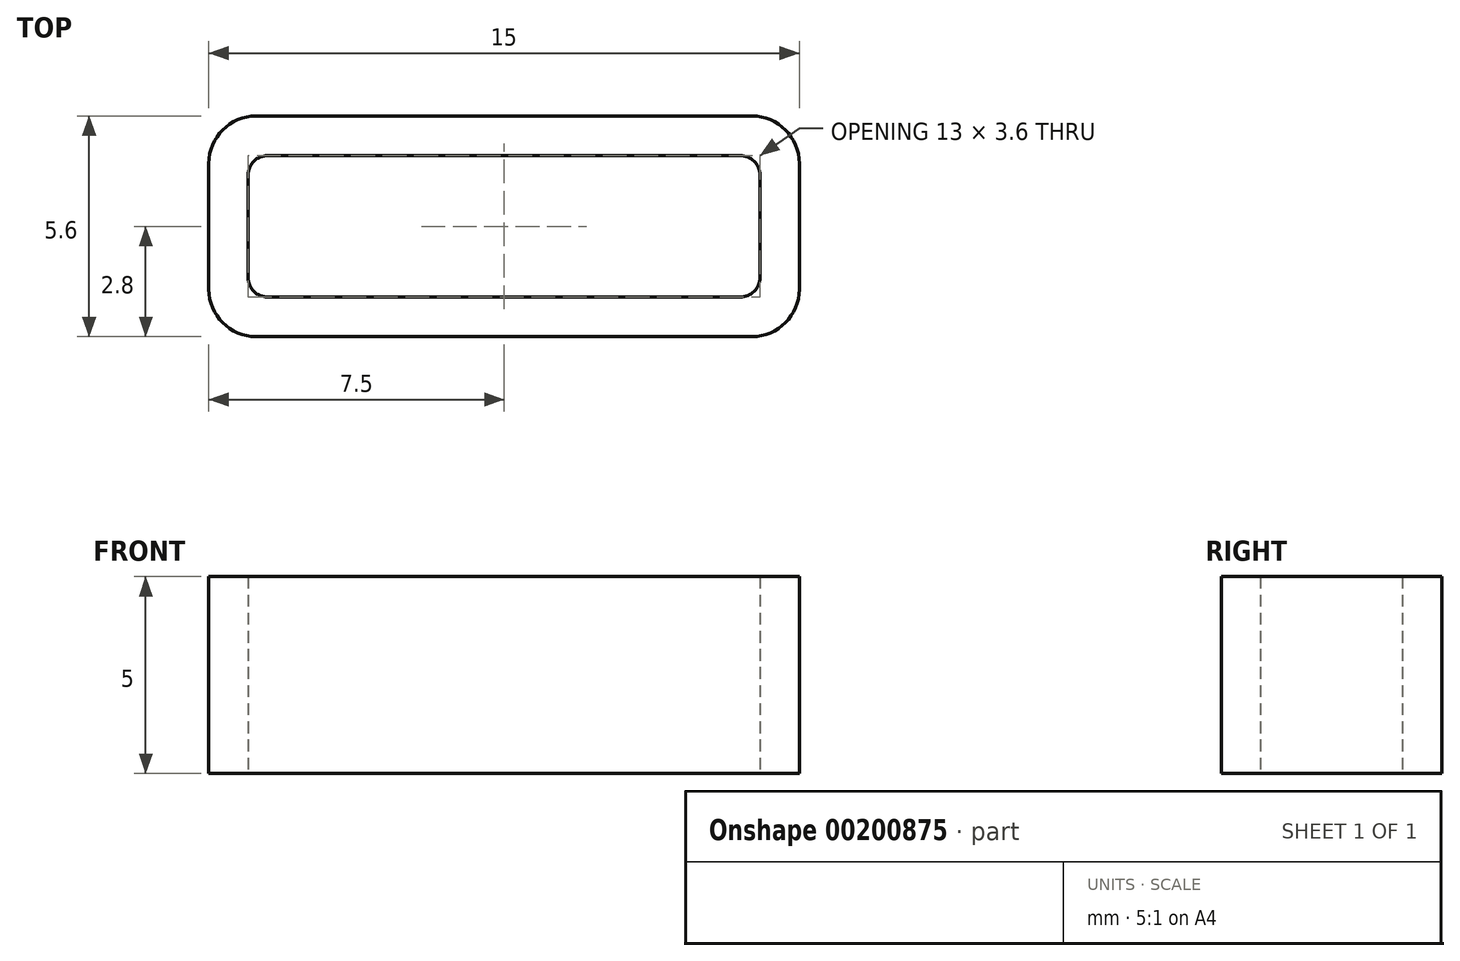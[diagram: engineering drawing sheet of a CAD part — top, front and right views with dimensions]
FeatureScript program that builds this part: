
annotation { "Feature Type Name" : "Feature", "Feature Type Description" : "" }
export const myFeature = defineFeature(function(context is Context, id is Id, definition is map)
    precondition{}
    {
        {
            var Q0;
            Q0=qCreatedBy(makeId("Top.planeOp"),FACE);
            var sketch = newSketch(context, id + "F0", { "sketchPlane" : qUnion([Q0])});
            skLineSegment(sketch, "E0.bottom", {"start": v(-6.5, 1.8) * mm, "end": v(6.5, 1.8) * mm});
            skLineSegment(sketch, "E0.top", {"start": v(-6.5, -1.8) * mm, "end": v(6.5, -1.8) * mm});
            skLineSegment(sketch, "E0.left", {"start": v(-6.5, 1.8) * mm, "end": v(-6.5, -1.8) * mm});
            skLineSegment(sketch, "E0.right", {"start": v(6.5, 1.8) * mm, "end": v(6.5, -1.8) * mm});
            skPoint(sketch, "E0.middle", {"position": v(0, 0) * mm});
            skLineSegment(sketch, "E1.bottom", {"start": v(-7.5, 2.8) * mm, "end": v(7.5, 2.8) * mm});
            skLineSegment(sketch, "E1.top", {"start": v(-7.5, -2.8) * mm, "end": v(7.5, -2.8) * mm});
            skLineSegment(sketch, "E1.left", {"start": v(-7.5, 2.8) * mm, "end": v(-7.5, -2.8) * mm});
            skLineSegment(sketch, "E1.right", {"start": v(7.5, 2.8) * mm, "end": v(7.5, -2.8) * mm});
            skLineSegment(sketch, "E2", {"start": v(-6.5, 1.8) * mm, "end": v(-6.5, 2.8) * mm, "construction": true});
            skLineSegment(sketch, "E3", {"start": v(-6.5, 1.8) * mm, "end": v(-7.5, 1.8) * mm, "construction": true});
            skLineSegment(sketch, "E4", {"start": v(6.5, -1.8) * mm, "end": v(6.5, -2.8) * mm, "construction": true});
            skLineSegment(sketch, "E5", {"start": v(6.5, -1.8) * mm, "end": v(7.5, -1.8) * mm, "construction": true});
            skSolve(sketch);
        }
        {
            var Q0;
            Q0=makeQuery(id+"F0.imprint","IMPRINT",FACE,{"disambiguationData":[TD([[makeQuery(id+"F0.imprint","IMPRINT",EDGE,{"derivedFrom":sQuery(id+"F0.wireOp",EDGE,"E0.bottom")}),1.0]])]});
            extrude(context, id + "F1", {"entities" : qUnion([Q0]), "depth" : 5 * mm});
        }
        {
            var Q0;
            Q0=makeQuery(id+"F1.opExtrude","SWEPT_EDGE",EDGE,{"disambiguationData":[OSD([sQuery(id+"F0.wireOp",EDGE,"E1.top"),sQuery(id+"F0.wireOp",EDGE,"E1.left")])]});
            var Q1;
            Q1=makeQuery(id+"F1.opExtrude","SWEPT_EDGE",EDGE,{"disambiguationData":[OSD([sQuery(id+"F0.wireOp",EDGE,"E1.bottom"),sQuery(id+"F0.wireOp",EDGE,"E1.left")])]});
            var Q2;
            Q2=makeQuery(id+"F1.opExtrude","SWEPT_EDGE",EDGE,{"disambiguationData":[OSD([sQuery(id+"F0.wireOp",EDGE,"E1.top"),sQuery(id+"F0.wireOp",EDGE,"E1.right")])]});
            var Q3;
            Q3=makeQuery(id+"F1.opExtrude","SWEPT_EDGE",EDGE,{"disambiguationData":[OSD([sQuery(id+"F0.wireOp",EDGE,"E1.bottom"),sQuery(id+"F0.wireOp",EDGE,"E1.right")])]});
            fillet(context, id + "F2", {"entities" : qUnion([Q0, Q1, Q2, Q3]), "radius" : 1.2 * mm, "tangentPropagation" : true, "allowEdgeOverflow" : false});
        }
        {
            var Q0;
            Q0=makeQuery(id+"F1.opExtrude","SWEPT_EDGE",EDGE,{"disambiguationData":[OSD([sQuery(id+"F0.wireOp",EDGE,"E0.top"),sQuery(id+"F0.wireOp",EDGE,"E0.left")])]});
            var Q1;
            Q1=makeQuery(id+"F1.opExtrude","SWEPT_EDGE",EDGE,{"disambiguationData":[OSD([sQuery(id+"F0.wireOp",EDGE,"E0.bottom"),sQuery(id+"F0.wireOp",EDGE,"E0.left")])]});
            var Q2;
            Q2=makeQuery(id+"F1.opExtrude","SWEPT_EDGE",EDGE,{"disambiguationData":[OSD([sQuery(id+"F0.wireOp",EDGE,"E0.bottom"),sQuery(id+"F0.wireOp",EDGE,"E0.right")])]});
            var Q3;
            Q3=makeQuery(id+"F1.opExtrude","SWEPT_EDGE",EDGE,{"disambiguationData":[OSD([sQuery(id+"F0.wireOp",EDGE,"E0.top"),sQuery(id+"F0.wireOp",EDGE,"E0.right")])]});
            fillet(context, id + "F3", {"entities" : qUnion([Q0, Q1, Q2, Q3]), "radius" : 0.5 * mm, "allowEdgeOverflow" : false});
        }
    });
